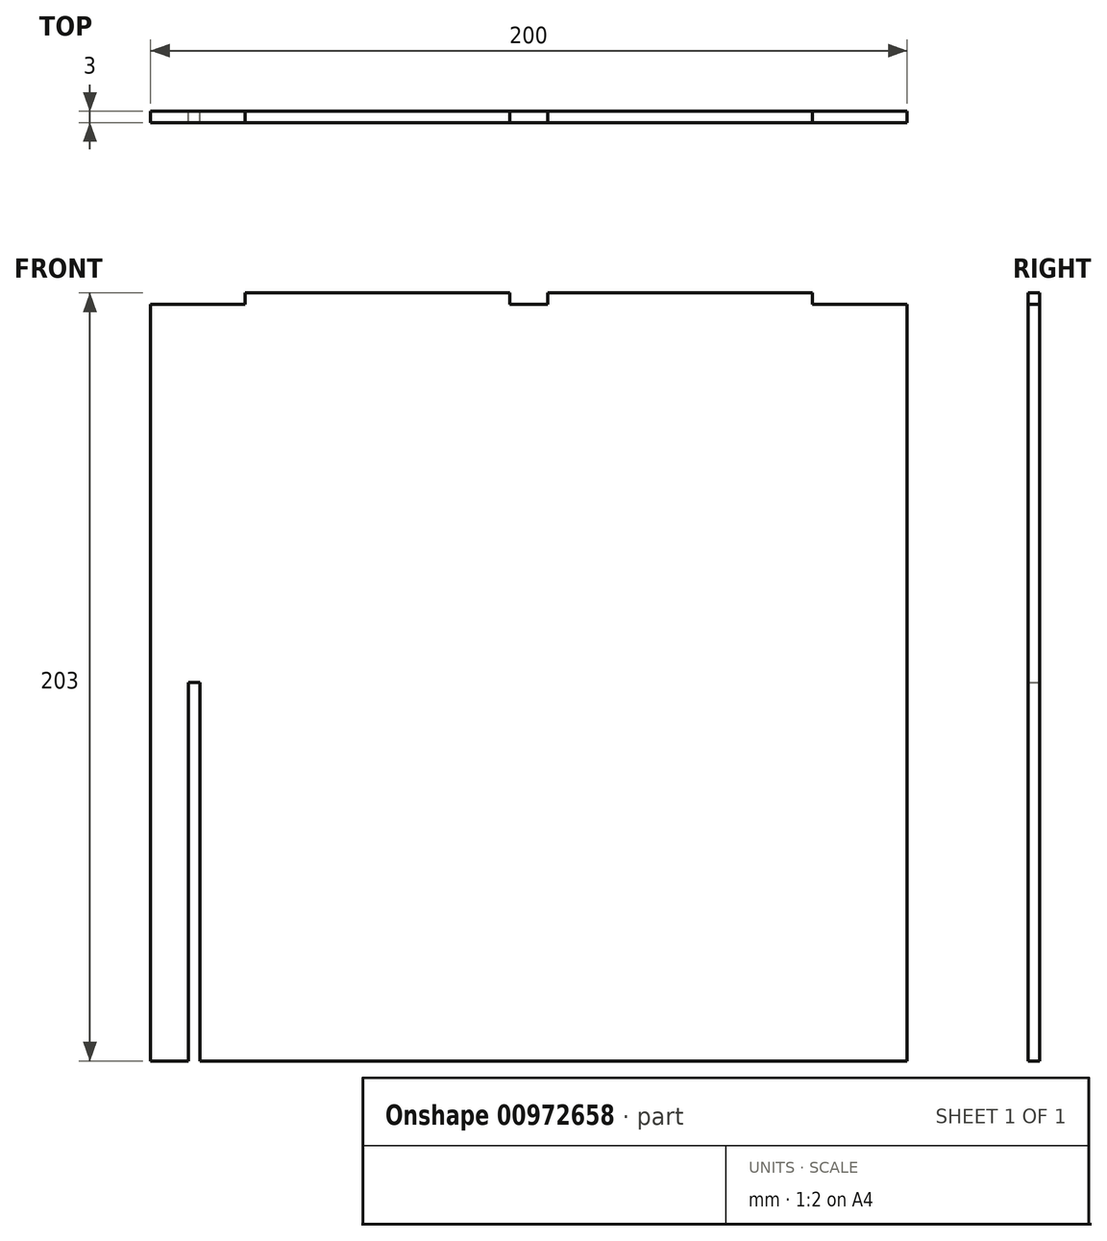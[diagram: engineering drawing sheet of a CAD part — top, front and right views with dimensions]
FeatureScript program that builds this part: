
annotation { "Feature Type Name" : "Feature", "Feature Type Description" : "" }
export const myFeature = defineFeature(function(context is Context, id is Id, definition is map)
    precondition{}
    {
        {
            var Q0;
            Q0=qCreatedBy(makeId("Front.planeOp"),FACE);
            var sketch = newSketch(context, id + "F0", { "sketchPlane" : qUnion([Q0])});
            skLineSegment(sketch, "E0.bottom", {"start": v(-81.86, 146.71) * mm, "end": v(118.14, 146.71) * mm});
            skLineSegment(sketch, "E0.top", {"start": v(-81.86, -53.29) * mm, "end": v(118.14, -53.29) * mm});
            skLineSegment(sketch, "E0.left", {"start": v(-81.86, 146.71) * mm, "end": v(-81.86, -53.29) * mm});
            skLineSegment(sketch, "E0.right", {"start": v(118.14, 146.71) * mm, "end": v(118.14, -53.29) * mm});
            skLineSegment(sketch, "E1.bottom", {"start": v(-71.86, -53.29) * mm, "end": v(-68.86, -53.29) * mm});
            skLineSegment(sketch, "E1.top", {"start": v(-71.86, 46.71) * mm, "end": v(-68.86, 46.71) * mm});
            skLineSegment(sketch, "E1.left", {"start": v(-71.86, -53.29) * mm, "end": v(-71.86, 46.71) * mm});
            skLineSegment(sketch, "E1.right", {"start": v(-68.86, -53.29) * mm, "end": v(-68.86, 46.71) * mm});
            skPoint(sketch, "E2", {"position": v(-81.86, 46.71) * mm});
            skLineSegment(sketch, "E3.left", {"start": v(118.14, -43.29) * mm, "end": v(118.14, -40.29) * mm});
            skPoint(sketch, "E4", {"position": v(18.14, -53.29) * mm});
            skLineSegment(sketch, "E5", {"start": v(-56.86, 146.71) * mm, "end": v(-56.86, 149.71) * mm});
            skLineSegment(sketch, "E6", {"start": v(-56.86, 149.71) * mm, "end": v(13.14, 149.71) * mm});
            skLineSegment(sketch, "E7", {"start": v(13.14, 149.71) * mm, "end": v(13.14, 146.71) * mm});
            skLineSegment(sketch, "E8", {"start": v(23.14, 146.71) * mm, "end": v(23.14, 149.71) * mm});
            skLineSegment(sketch, "E9", {"start": v(23.14, 149.71) * mm, "end": v(93.14, 149.71) * mm});
            skLineSegment(sketch, "E10", {"start": v(93.14, 149.71) * mm, "end": v(93.14, 146.71) * mm});
            skSolve(sketch);
        }
        {
            var Q0;
            {var subQ7=sQuery(id+"F0.wireOp",EDGE,"E0.bottom");Q0=makeQuery(id+"F0.imprint","IMPRINT",FACE,{"disambiguationData":[TD([[makeQuery(id+"F0.imprint","IMPRINT",EDGE,{"derivedFrom":subQ7}),-1.0]])]});}
            var Q1;
            {var subQ0=sQuery(id+"F0.wireOp",EDGE,"E5");Q1=makeQuery(id+"F0.imprint","IMPRINT",FACE,{"disambiguationData":[TD([[makeQuery(id+"F0.imprint","IMPRINT",EDGE,{"derivedFrom":subQ0}),-1.0]])]});}
            var Q2;
            {var subQ0=sQuery(id+"F0.wireOp",EDGE,"E8");Q2=makeQuery(id+"F0.imprint","IMPRINT",FACE,{"disambiguationData":[TD([[makeQuery(id+"F0.imprint","IMPRINT",EDGE,{"derivedFrom":subQ0}),-1.0]])]});}
            extrude(context, id + "F1", {"entities" : qUnion([Q0, Q1, Q2]), "depth" : 3 * mm, "offsetDistance" : 25 * mm});
        }
    });
